# Revit family: BuzziPebl Light - Wall Hosted
name_source: partatom
category: Lighting Fixtures
revit_build: Autodesk Revit 2018 (Build: 20170223_1515(x64)
units: mm (PartAtom-declared; Revit-internal decimal feet)

## family parameters
Always vertical = Yes
Cut with Voids When Loaded = No
Host = Wall
Light Source = Yes
OmniClass Number = 23.80.70.00
OmniClass Title = Lighting
Part Type = Normal
Room Calculation Point = No
Round Connector Dimension = Use Diameter
Shared = No

## types (4) — shared parameters
Color Filter = 16777215
Dimming Lamp Color Temperature Shift = <None>
Emit Shape Visible in Rendering = No

## per-type parameters (varying)
| type | Diameter | Emit from Circle Diameter | Light Source Symbol Size | Pebl Visibility |
| Pebl One - Medium | 2' - 6 25/32" | 2' - 6 25/32" | 1' - 3 13/32" | 0 |
| Pebl One - Large | 3' - 9 9/32" | 3' - 9 9/32" | 1' - 10 5/8" | 0 |
| Pebl Two - Medium | 2' - 6 25/32" | 2' - 6 25/32" | 1' - 3 13/32" | 1 |
| Pebl Two - Large | 3' - 9 9/32" | 3' - 9 9/32" | 1' - 10 5/8" | 2 |

## geometry (parser evidence)
native form markers: Sweep x4
no freeform markers — native parametric forms only
